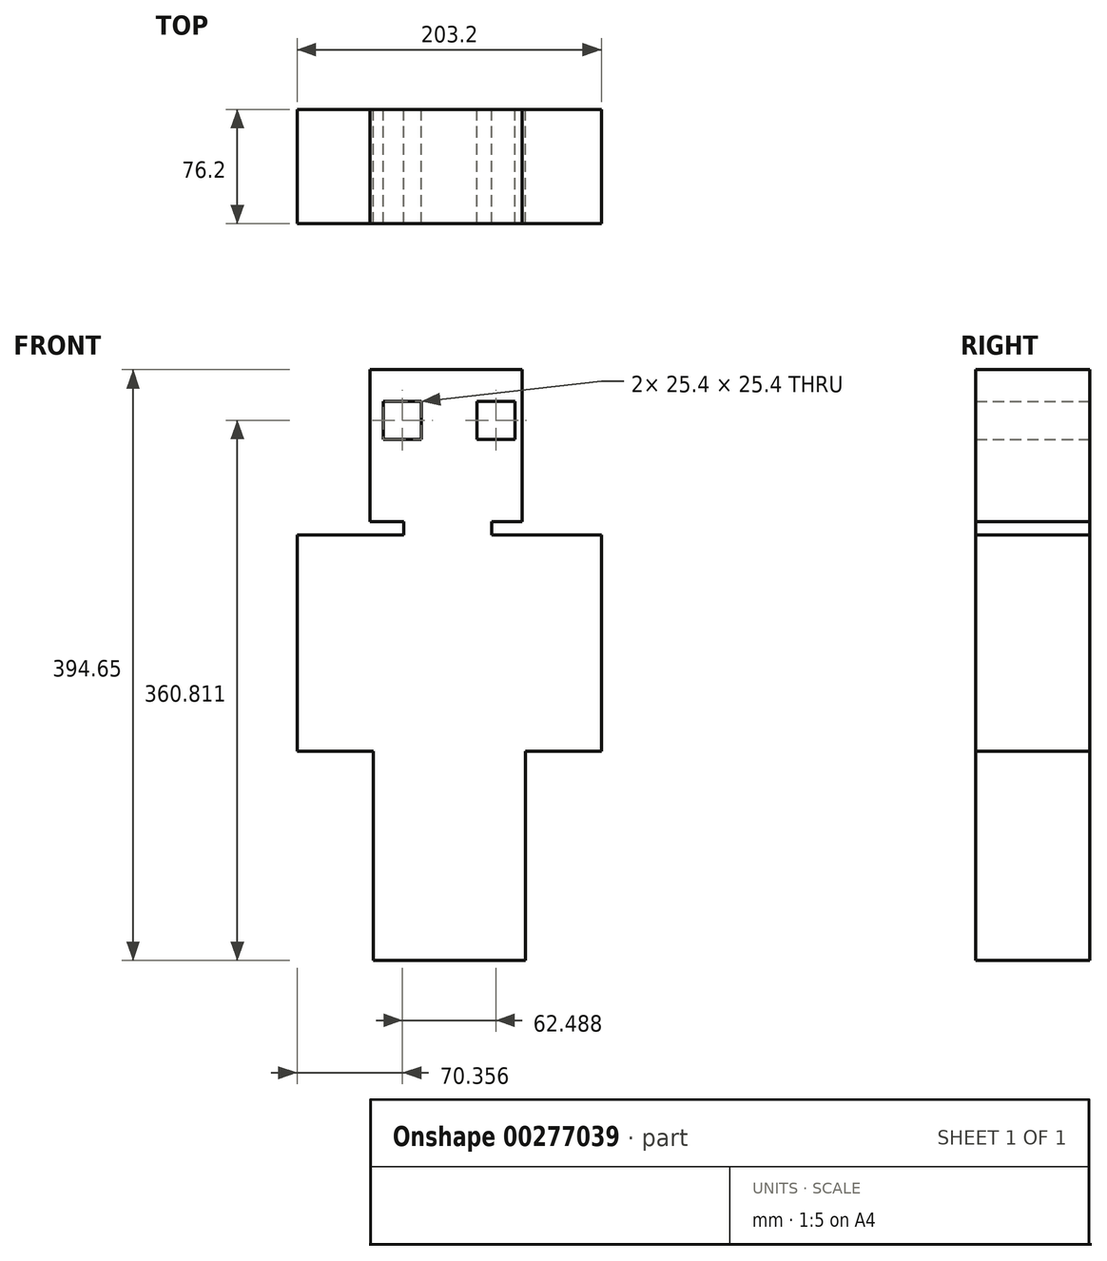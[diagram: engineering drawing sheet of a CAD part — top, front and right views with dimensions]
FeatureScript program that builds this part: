
annotation { "Feature Type Name" : "Feature", "Feature Type Description" : "" }
export const myFeature = defineFeature(function(context is Context, id is Id, definition is map)
    precondition{}
    {
        {
            var Q0;
            Q0=qCreatedBy(makeId("Front.planeOp"),FACE);
            var sketch = newSketch(context, id + "F0", { "sketchPlane" : qUnion([Q0])});
            skLineSegment(sketch, "E0.bottom", {"start": v(-52.85, -9.83) * mm, "end": v(48.75, -9.83) * mm});
            skLineSegment(sketch, "E0.top", {"start": v(-52.85, 91.77) * mm, "end": v(48.75, 91.77) * mm});
            skLineSegment(sketch, "E0.left", {"start": v(-52.85, -9.83) * mm, "end": v(-52.85, 91.77) * mm});
            skLineSegment(sketch, "E0.right", {"start": v(48.75, -9.83) * mm, "end": v(48.75, 91.77) * mm});
            skLineSegment(sketch, "E1.bottom", {"start": v(-30.46, -9.83) * mm, "end": v(28.46, -9.83) * mm});
            skLineSegment(sketch, "E1.top", {"start": v(-30.46, -20) * mm, "end": v(28.46, -20) * mm});
            skLineSegment(sketch, "E1.left", {"start": v(-30.46, -9.83) * mm, "end": v(-30.46, -20) * mm});
            skLineSegment(sketch, "E1.right", {"start": v(28.46, -9.83) * mm, "end": v(28.46, -20) * mm});
            skLineSegment(sketch, "E2.bottom", {"start": v(-50.8, -18.8) * mm, "end": v(53.15, -18.8) * mm});
            skLineSegment(sketch, "E2.top", {"start": v(-50.8, -162.99) * mm, "end": v(50.8, -162.99) * mm});
            skLineSegment(sketch, "E2.left", {"start": v(-50.8, -18.8) * mm, "end": v(-50.8, -162.99) * mm});
            skLineSegment(sketch, "E3.bottom", {"start": v(-50.8, -18.8) * mm, "end": v(-101.6, -18.8) * mm});
            skLineSegment(sketch, "E3.top", {"start": v(-50.8, -162.99) * mm, "end": v(-101.6, -162.99) * mm});
            skLineSegment(sketch, "E3.right", {"start": v(-101.6, -18.8) * mm, "end": v(-101.6, -162.99) * mm});
            skLineSegment(sketch, "E4.left", {"start": v(-50.8, -162.99) * mm, "end": v(-50.8, -162.99) * mm});
            skLineSegment(sketch, "E4.right", {"start": v(0, -161.27) * mm, "end": v(0, -162.99) * mm});
            skLineSegment(sketch, "E5.bottom", {"start": v(-43.94, 45.23) * mm, "end": v(-18.54, 45.23) * mm});
            skLineSegment(sketch, "E5.top", {"start": v(-43.94, 70.63) * mm, "end": v(-18.54, 70.63) * mm});
            skLineSegment(sketch, "E5.left", {"start": v(-43.94, 45.23) * mm, "end": v(-43.94, 70.63) * mm});
            skLineSegment(sketch, "E5.right", {"start": v(-18.54, 45.23) * mm, "end": v(-18.54, 70.63) * mm});
            skLineSegment(sketch, "E6.MirrorCS", {"start": v(18.54, 45.23) * mm, "end": v(18.54, 70.63) * mm});
            skLineSegment(sketch, "E7.MirrorCS", {"start": v(43.94, 70.63) * mm, "end": v(18.54, 70.63) * mm});
            skLineSegment(sketch, "E8.MirrorCS", {"start": v(43.94, 45.23) * mm, "end": v(43.94, 70.63) * mm});
            skLineSegment(sketch, "E9.MirrorCS", {"start": v(43.94, 45.23) * mm, "end": v(18.54, 45.23) * mm});
            skLineSegment(sketch, "E10", {"start": v(-52.85, 65.55) * mm, "end": v(-47.36, 65.55) * mm});
            skLineSegment(sketch, "E11", {"start": v(-47.36, 65.55) * mm, "end": v(-47.36, 79.68) * mm});
            skLineSegment(sketch, "E12", {"start": v(-47.36, 79.68) * mm, "end": v(-20.7, 79.68) * mm});
            skLineSegment(sketch, "E13", {"start": v(-20.7, 79.68) * mm, "end": v(-20.7, 71.69) * mm});
            skLineSegment(sketch, "E14", {"start": v(-20.7, 71.69) * mm, "end": v(8.88, 71.69) * mm});
            skLineSegment(sketch, "E15", {"start": v(8.88, 71.69) * mm, "end": v(8.88, 75.95) * mm});
            skLineSegment(sketch, "E16", {"start": v(8.88, 75.95) * mm, "end": v(33.4, 75.95) * mm});
            skLineSegment(sketch, "E17", {"start": v(33.4, 75.95) * mm, "end": v(33.4, 71.42) * mm});
            skLineSegment(sketch, "E18", {"start": v(33.4, 71.42) * mm, "end": v(48.75, 71.42) * mm});
            skLineSegment(sketch, "E19", {"start": v(-31.24, 70.63) * mm, "end": v(-31.24, 53.83) * mm});
            skLineSegment(sketch, "E20", {"start": v(-31.24, 53.83) * mm, "end": v(-18.54, 53.83) * mm});
            skLineSegment(sketch, "E21", {"start": v(31.24, 70.63) * mm, "end": v(31.24, 53.83) * mm});
            skLineSegment(sketch, "E22", {"start": v(31.24, 53.83) * mm, "end": v(43.94, 53.83) * mm});
            skLineSegment(sketch, "E23", {"start": v(-101.6, -112.64) * mm, "end": v(-50.8, -112.64) * mm});
            skLineSegment(sketch, "E24.MirrorCS", {"start": v(101.6, -112.64) * mm, "end": v(50.8, -112.64) * mm});
            skLineSegment(sketch, "E25.MirrorCS", {"start": v(101.6, -18.8) * mm, "end": v(101.6, -162.99) * mm});
            skLineSegment(sketch, "E26.MirrorCS", {"start": v(50.8, -18.8) * mm, "end": v(50.8, -162.99) * mm});
            skLineSegment(sketch, "E27.MirrorCS", {"start": v(50.8, -18.8) * mm, "end": v(101.6, -18.8) * mm});
            skLineSegment(sketch, "E28", {"start": v(50.8, -162.99) * mm, "end": v(101.6, -162.99) * mm});
            skLineSegment(sketch, "E29.bottom", {"start": v(-50.8, -162.99) * mm, "end": v(0, -162.99) * mm});
            skLineSegment(sketch, "E29.left", {"start": v(-50.8, -162.99) * mm, "end": v(-50.8, -272.2) * mm});
            skLineSegment(sketch, "E29.right", {"start": v(0, -162.99) * mm, "end": v(0, -272.2) * mm});
            skLineSegment(sketch, "E30.bottom", {"start": v(50.8, -162.99) * mm, "end": v(0, -162.99) * mm});
            skLineSegment(sketch, "E30.left", {"start": v(50.8, -162.99) * mm, "end": v(50.8, -272.2) * mm});
            skLineSegment(sketch, "E31", {"start": v(-50.8, -272.2) * mm, "end": v(0, -272.2) * mm});
            skLineSegment(sketch, "E32", {"start": v(0, -272.2) * mm, "end": v(50.8, -272.2) * mm});
            skLineSegment(sketch, "E33.top", {"start": v(-50.8, -302.88) * mm, "end": v(0, -302.88) * mm});
            skLineSegment(sketch, "E33.left", {"start": v(-50.8, -272.2) * mm, "end": v(-50.8, -302.88) * mm});
            skLineSegment(sketch, "E33.right", {"start": v(0, -272.2) * mm, "end": v(0, -302.88) * mm});
            skLineSegment(sketch, "E34.bottom", {"start": v(50.8, -272.2) * mm, "end": v(0, -272.2) * mm});
            skLineSegment(sketch, "E34.top", {"start": v(50.8, -302.88) * mm, "end": v(0, -302.88) * mm});
            skLineSegment(sketch, "E34.left", {"start": v(50.8, -272.2) * mm, "end": v(50.8, -302.88) * mm});
            skSolve(sketch);
        }
        {
            var Q0;
            Q0 = qSketchRegion(id + "F0", true);
            extrude(context, id + "F1", {"entities" : qUnion([Q0]), "depth" : 76.2 * mm, "symmetric" : true});
        }
    });
